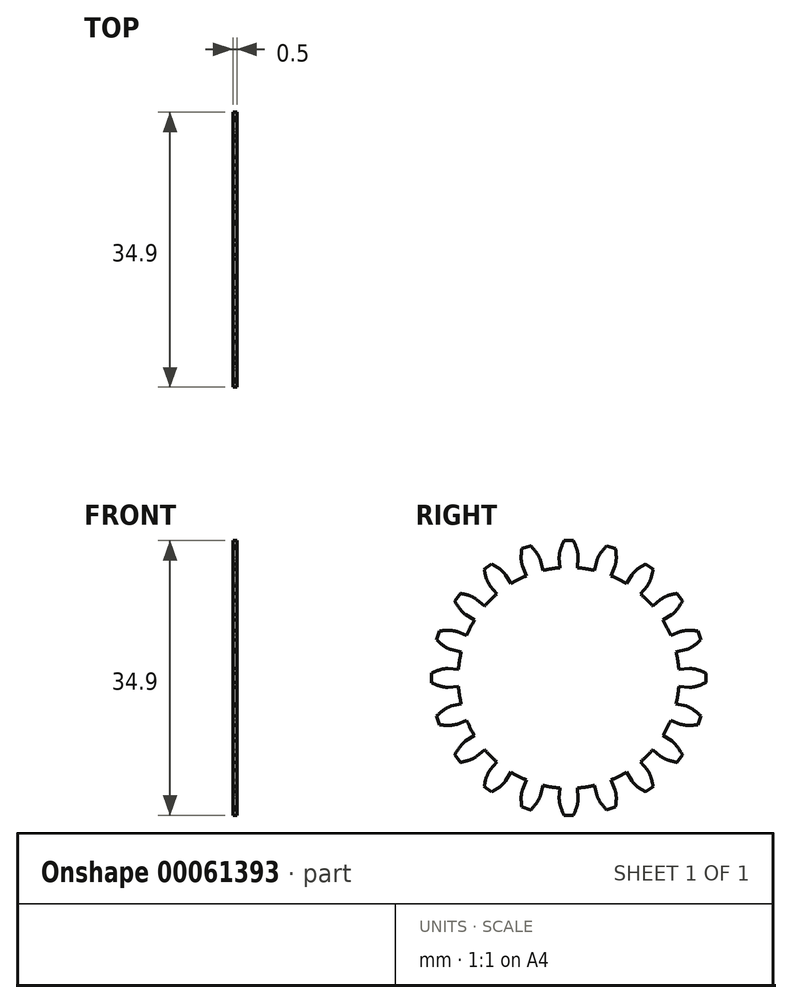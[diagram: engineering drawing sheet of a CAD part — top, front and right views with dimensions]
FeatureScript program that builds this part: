
annotation { "Feature Type Name" : "Feature", "Feature Type Description" : "" }
export const myFeature = defineFeature(function(context is Context, id is Id, definition is map)
    precondition{}
    {
        {
            assignVariable(context, id + "F0", {"name" : "NumberTeeth", "anyValue" : 20});
        }
        {
            assignVariable(context, id + "F1", {"name" : "GearThickness", "anyValue" : .5});
        }
        {
            var Q0;
            Q0=qCreatedBy(makeId("Right.planeOp"),FACE);
            var sketch = newSketch(context, id + "F2", { "sketchPlane" : qUnion([Q0])});
            skCircle(sketch, "E0", {"center": v(0, 0) * mm, "radius": 15.37 * mm, "construction": true});
            skCircle(sketch, "E1", {"center": v(0, 0) * mm, "radius": 15.88 * mm, "construction": true});
            skCircle(sketch, "E2", {"center": v(0, 0) * mm, "radius": 17.46 * mm, "construction": true});
            skCircle(sketch, "E3", {"center": v(0, 0) * mm, "radius": 14.04 * mm, "construction": true});
            skLineSegment(sketch, "E4", {"start": v(0, 0) * mm, "end": v(-14.04, 0) * mm, "construction": true});
            skLineSegment(sketch, "E5", {"start": v(0, 0) * mm, "end": v(-15.32, -1.2) * mm, "construction": true});
            skLineSegment(sketch, "E6.1.0", {"start": v(0, 0) * mm, "end": v(-15.34, 0.86) * mm, "construction": true});
            skLineSegment(sketch, "E6.2.0", {"start": v(0, 0) * mm, "end": v(-15.09, 2.92) * mm, "construction": true});
            skLineSegment(sketch, "E6.3.0", {"start": v(0, 0) * mm, "end": v(-14.56, 4.92) * mm, "construction": true});
            skLineSegment(sketch, "E6.4.0", {"start": v(0, 0) * mm, "end": v(-13.77, 6.83) * mm, "construction": true});
            skLineSegment(sketch, "E6.anchor2", {"start": v(0, 0) * mm, "end": v(-13.77, 6.83) * mm, "construction": true});
            skLineSegment(sketch, "E7", {"start": v(0, 0) * mm, "end": v(-15.34, -1) * mm, "construction": true});
            skLineSegment(sketch, "E8", {"start": v(0, 0) * mm, "end": v(-13.86, 6.65) * mm, "construction": true});
            skLineSegment(sketch, "E9", {"start": v(-13.77, 6.83) * mm, "end": v(-17.45, -0.6) * mm, "construction": true});
            skLineSegment(sketch, "E10", {"start": v(-13.86, 6.65) * mm, "end": v(-17.35, -0.64) * mm, "construction": true});
            skLineSegment(sketch, "E11", {"start": v(-14.56, 4.92) * mm, "end": v(-16.55, -0.97) * mm, "construction": true});
            skLineSegment(sketch, "E12", {"start": v(-15.09, 2.92) * mm, "end": v(-15.88, -1.15) * mm, "construction": true});
            skLineSegment(sketch, "E13", {"start": v(-15.34, 0.86) * mm, "end": v(-15.46, -1.2) * mm, "construction": true});
            skLineSegment(sketch, "E14", {"start": v(-15.34, -1) * mm, "end": v(-15.32, -1.2) * mm, "construction": true});
            skFitSpline(sketch, "E15", {"points": [v(-15.32, -1.2) * mm, v(-15.88, -1.15) * mm, v(-16.55, -0.97) * mm, v(-17.45, -0.6) * mm], "startDerivative": vector(-1.44, 0.02) * mm, "endDerivative": vector(-0.77, 0.38) * mm});
            skLineSegment(sketch, "E16", {"start": v(-14, -1.1) * mm, "end": v(-15.32, -1.2) * mm});
            skLineSegment(sketch, "E17.MirrorCS", {"start": v(-14, 1.1) * mm, "end": v(-15.32, 1.2) * mm});
            skFitSpline(sketch, "E18.MirrorCS", {"points": [v(-15.32, 1.2) * mm, v(-15.88, 1.15) * mm, v(-16.55, 0.97) * mm, v(-17.45, 0.6) * mm], "startDerivative": vector(-1.44, -0.02) * mm, "endDerivative": vector(-0.77, -0.38) * mm});
            skLineSegment(sketch, "E19", {"start": v(-17.45, 0.6) * mm, "end": v(-17.45, -0.6) * mm});
            skArc(sketch, "E20", {"start": v(-14, -1.1) * mm, "mid": v(14.04, 0) * mm, "end": v(-14, 1.1) * mm});
            skSolve(sketch);
        }
        {
            var Q0;
            Q0=makeQuery(id+"F2.imprint","IMPRINT",FACE,{"disambiguationData":[TD([[makeQuery(id+"F2.imprint","IMPRINT",EDGE,{"derivedFrom":sQuery(id+"F2.wireOp",EDGE,"E15")}),-1.0]])]});
            extrude(context, id + "F3", {"entities" : qUnion([Q0]), "depth" : (getVariable(context, 'GearThickness')) * mm});
        }
        {
            var Q0;
            Q0=makeQuery(id+"F3.opExtrude","SWEPT_FACE",FACE,{"disambiguationData":[OSD([sQuery(id+"F2.wireOp",EDGE,"E17.MirrorCS")])]});
            var Q1;
            Q1=makeQuery(id+"F3.opExtrude","SWEPT_FACE",FACE,{"disambiguationData":[OSD([sQuery(id+"F2.wireOp",EDGE,"E18.MirrorCS")])]});
            var Q2;
            Q2=makeQuery(id+"F3.opExtrude","SWEPT_FACE",FACE,{"disambiguationData":[OSD([sQuery(id+"F2.wireOp",EDGE,"E19")])]});
            var Q3;
            Q3=makeQuery(id+"F3.opExtrude","SWEPT_FACE",FACE,{"disambiguationData":[OSD([sQuery(id+"F2.wireOp",EDGE,"E15")])]});
            var Q4;
            Q4=makeQuery(id+"F3.opExtrude","SWEPT_FACE",FACE,{"disambiguationData":[OSD([sQuery(id+"F2.wireOp",EDGE,"E16")])]});
            var Q5;
            Q5=makeQuery(id+"F3.opExtrude","SWEPT_FACE",FACE,{"disambiguationData":[OSD([sQuery(id+"F2.wireOp",EDGE,"E20")])]});
            circularPattern(context, id + "F4", {"faces" : qUnion([Q0, Q1, Q2, Q3, Q4]), "axis" : qUnion([Q5]), "angle" : 360 * degree, "instanceCount" : round(getVariable(context, 'NumberTeeth')), "equalSpace" : true, "patternType" : PatternType.FACE});
        }
    });
